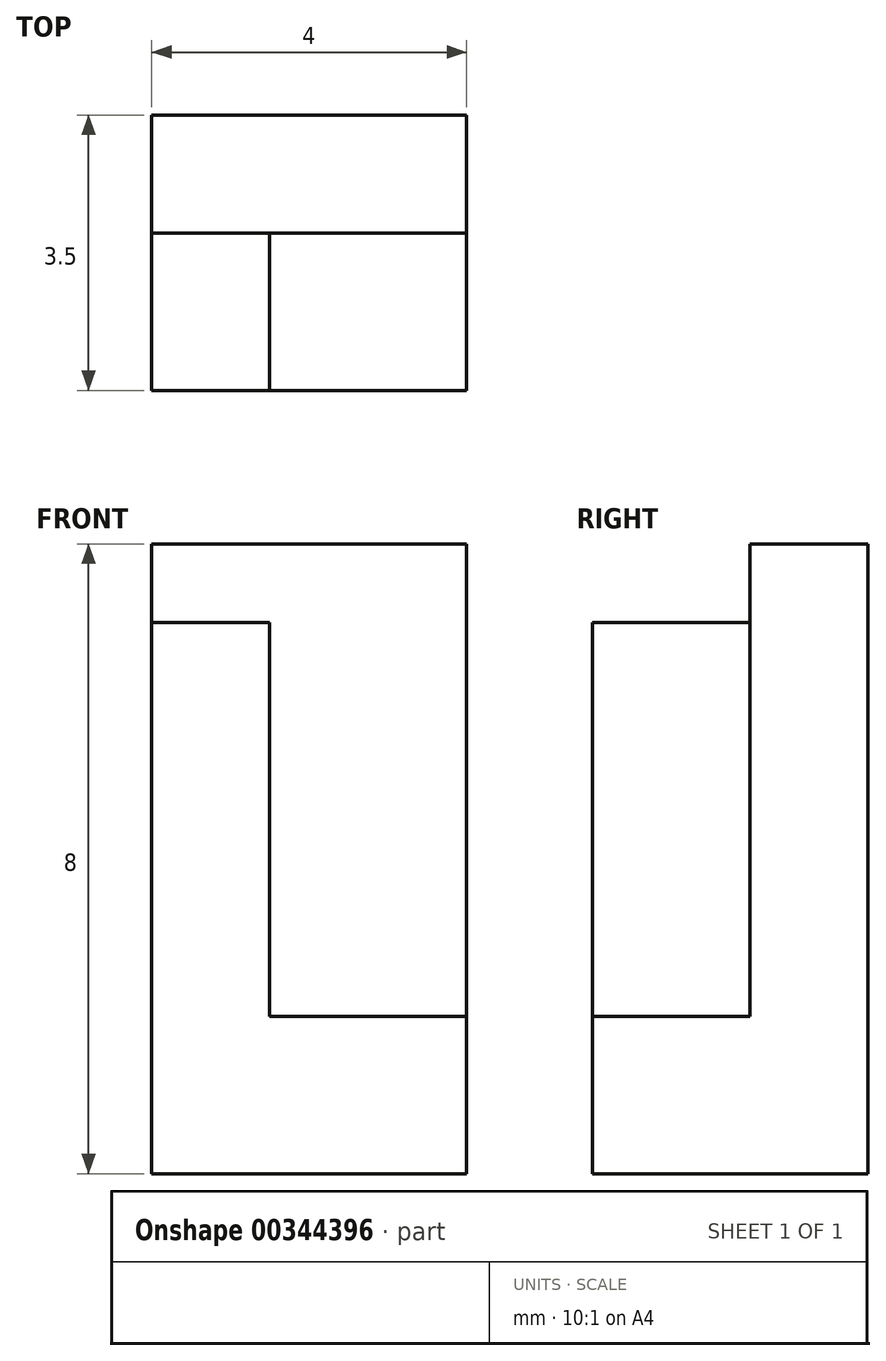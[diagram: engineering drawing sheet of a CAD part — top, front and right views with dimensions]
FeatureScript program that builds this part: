
annotation { "Feature Type Name" : "Feature", "Feature Type Description" : "" }
export const myFeature = defineFeature(function(context is Context, id is Id, definition is map)
    precondition{}
    {
        {
            var Q0;
            Q0=qCreatedBy(makeId("Top.planeOp"),FACE);
            var sketch = newSketch(context, id + "F0", { "sketchPlane" : qUnion([Q0])});
            skLineSegment(sketch, "E0.bottom", {"start": v(0, 0) * mm, "end": v(-4, 0) * mm});
            skLineSegment(sketch, "E0.top", {"start": v(0, 3.5) * mm, "end": v(-4, 3.5) * mm});
            skLineSegment(sketch, "E0.left", {"start": v(0, 0) * mm, "end": v(0, 3.5) * mm});
            skLineSegment(sketch, "E0.right", {"start": v(-4, 0) * mm, "end": v(-4, 3.5) * mm});
            skLineSegment(sketch, "E1", {"start": v(-4, 2) * mm, "end": v(0, 2) * mm});
            skLineSegment(sketch, "E2", {"start": v(-2.5, 2) * mm, "end": v(-2.5, 0) * mm});
            skSolve(sketch);
        }
        {
            var Q0;
            {var subQ1=sQuery(id+"F0.wireOp",EDGE,"E0.top");Q0=makeQuery(id+"F0.imprint","IMPRINT",FACE,{"disambiguationData":[TD([[makeQuery(id+"F0.imprint","IMPRINT",EDGE,{"derivedFrom":subQ1}),1.0]])]});}
            extrude(context, id + "F1", {"entities" : qUnion([Q0]), "depth" : 8 * mm});
        }
        {
            var Q0;
            {var subQ3=sQuery(id+"F0.wireOp",EDGE,"E2");Q0=makeQuery(id+"F0.imprint","IMPRINT",FACE,{"disambiguationData":[TD([[makeQuery(id+"F0.imprint","IMPRINT",EDGE,{"derivedFrom":subQ3}),-1.0]])]});}
            extrude(context, id + "F2", {"entities" : qUnion([Q0]), "operationType" : NewBodyOperationType.ADD, "depth" : 7 * mm});
        }
        {
            var Q0;
            {var subQ3=sQuery(id+"F0.wireOp",EDGE,"E2");Q0=makeQuery(id+"F0.imprint","IMPRINT",FACE,{"disambiguationData":[TD([[makeQuery(id+"F0.imprint","IMPRINT",EDGE,{"derivedFrom":subQ3}),1.0]])]});}
            extrude(context, id + "F3", {"entities" : qUnion([Q0]), "operationType" : NewBodyOperationType.ADD, "depth" : 2 * mm});
        }
    });
